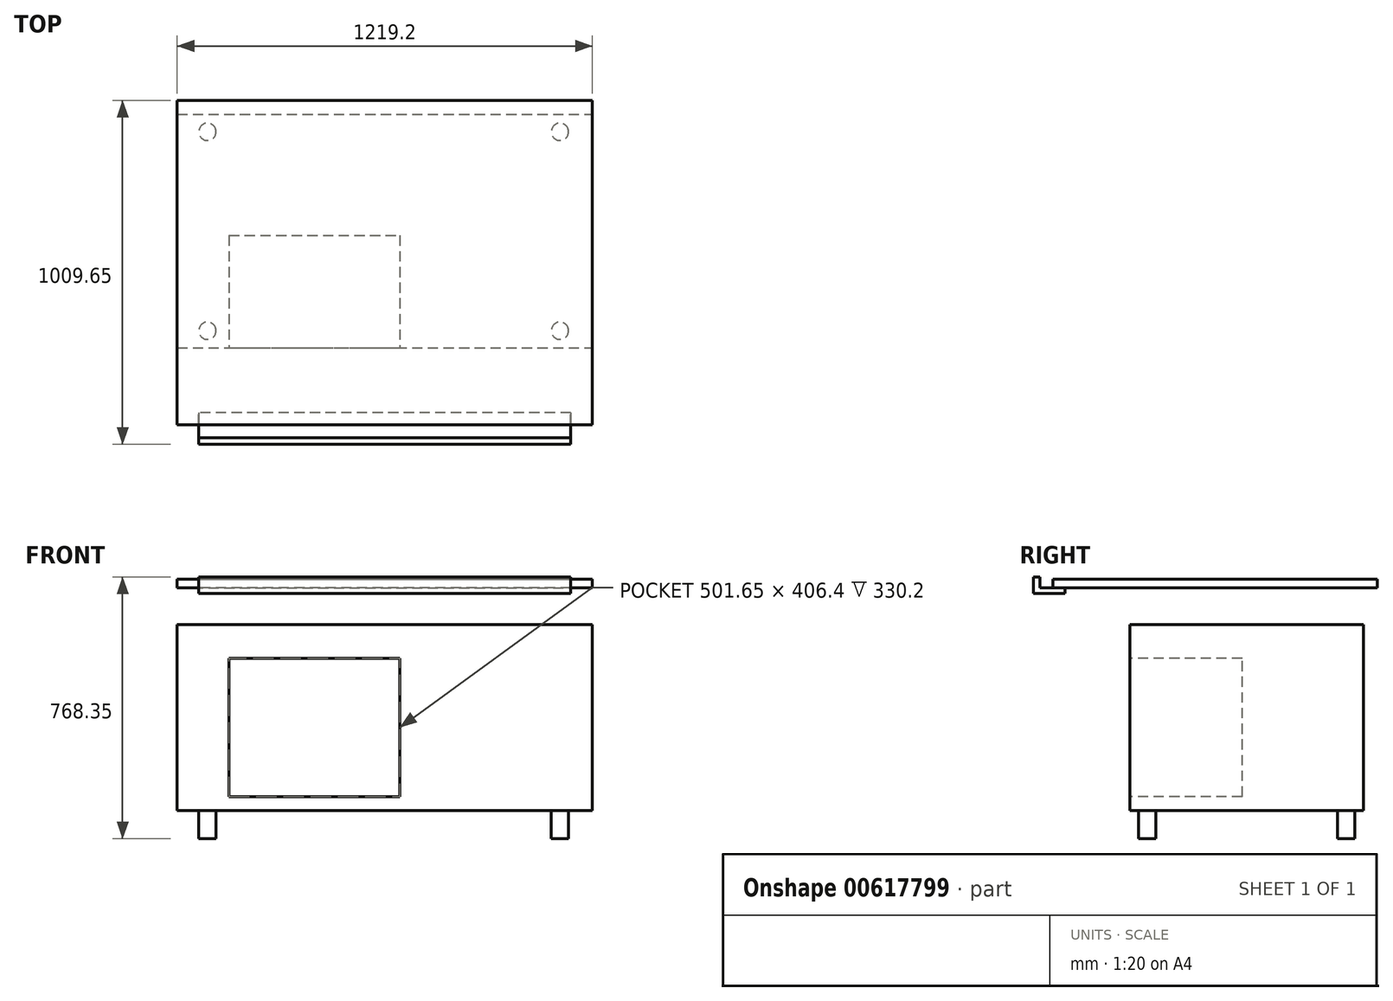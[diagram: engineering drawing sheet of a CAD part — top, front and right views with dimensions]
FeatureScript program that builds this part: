
annotation { "Feature Type Name" : "Feature", "Feature Type Description" : "" }
export const myFeature = defineFeature(function(context is Context, id is Id, definition is map)
    precondition{}
    {
        {
            var Q0;
            Q0=qCreatedBy(makeId("Top.planeOp"),FACE);
            var sketch = newSketch(context, id + "F0", { "sketchPlane" : qUnion([Q0])});
            skCircle(sketch, "E0", {"center": v(1035.05, 0) * mm, "radius": 25.4 * mm});
            skCircle(sketch, "E1", {"center": v(0, 0) * mm, "radius": 25.4 * mm});
            skCircle(sketch, "E2", {"center": v(1035.05, 584.2) * mm, "radius": 25.4 * mm});
            skCircle(sketch, "E3", {"center": v(0, 584.2) * mm, "radius": 25.4 * mm});
            skLineSegment(sketch, "E4.bottom", {"start": v(0, 584.2) * mm, "end": v(1035.05, 584.2) * mm, "construction": true});
            skLineSegment(sketch, "E4.top", {"start": v(0, 0) * mm, "end": v(1035.05, 0) * mm, "construction": true});
            skLineSegment(sketch, "E4.left", {"start": v(0, 584.2) * mm, "end": v(0, 0) * mm, "construction": true});
            skLineSegment(sketch, "E4.right", {"start": v(1035.05, 584.2) * mm, "end": v(1035.05, 0) * mm, "construction": true});
            skSolve(sketch);
        }
        {
            var Q0;
            Q0 = qSketchRegion(id + "F0", true);
            extrude(context, id + "F1", {"entities" : qUnion([Q0]), "depth" : 82.55 * mm, "offsetDistance" : 25.4 * mm});
        }
        {
            var Q0;
            Q0=makeQuery(id+"F1.opExtrude","CAP_FACE",FACE,{"disambiguationData":[OSD([sQuery(id+"F0.wireOp",EDGE,"E3")])],"isStart":false});
            var sketch = newSketch(context, id + "F2", { "sketchPlane" : qUnion([Q0])});
            skLineSegment(sketch, "E5.bottom", {"start": v(-88.9, 635) * mm, "end": v(1130.3, 635) * mm});
            skLineSegment(sketch, "E5.top", {"start": v(-88.9, -50.8) * mm, "end": v(1130.3, -50.8) * mm});
            skLineSegment(sketch, "E5.left", {"start": v(-88.9, 635) * mm, "end": v(-88.9, -50.8) * mm});
            skLineSegment(sketch, "E5.right", {"start": v(1130.3, 635) * mm, "end": v(1130.3, -50.8) * mm});
            skSolve(sketch);
        }
        {
            var Q0;
            Q0 = qSketchRegion(id + "F2", true);
            extrude(context, id + "F3", {"entities" : qUnion([Q0]), "depth" : 546.1 * mm, "offsetDistance" : 25.4 * mm});
        }
        {
            var Q0;
            Q0=makeQuery(id+"F3.opExtrude","SWEPT_FACE",FACE,{"disambiguationData":[OSD([sQuery(id+"F2.wireOp",EDGE,"E5.top")])]});
            var sketch = newSketch(context, id + "F4", { "sketchPlane" : qUnion([Q0])});
            skLineSegment(sketch, "E6.bottom", {"start": v(63.5, 123.83) * mm, "end": v(565.15, 123.83) * mm});
            skLineSegment(sketch, "E6.top", {"start": v(63.5, 530.22) * mm, "end": v(565.15, 530.22) * mm});
            skLineSegment(sketch, "E6.left", {"start": v(63.5, 123.83) * mm, "end": v(63.5, 530.23) * mm});
            skLineSegment(sketch, "E6.right", {"start": v(565.15, 123.83) * mm, "end": v(565.15, 530.23) * mm});
            skSolve(sketch);
        }
        {
            var Q0;
            Q0 = qSketchRegion(id + "F4", true);
            extrude(context, id + "F5", {"entities" : qUnion([Q0]), "operationType" : NewBodyOperationType.REMOVE, "oppositeDirection" : true, "depth" : 330.2 * mm, "offsetDistance" : 25.4 * mm});
        }
        {
            var Q0;
            Q0=qCreatedBy(makeId("Top.planeOp"),FACE);
            cPlane(context, id + "F6", {"entities" : qUnion([Q0]), "cplaneType" : CPlaneType.OFFSET, "offset" : 762 * mm, "width" : 152.4 * mm, "height" : 152.4 * mm});
        }
        {
            var Q0;
            Q0=qCreatedBy(id+"F6.planeOp",FACE);
            var sketch = newSketch(context, id + "F7", { "sketchPlane" : qUnion([Q0])});
            skLineSegment(sketch, "E7.bottom", {"start": v(-88.9, 676.28) * mm, "end": v(1130.3, 676.28) * mm});
            skLineSegment(sketch, "E7.top", {"start": v(-88.9, -276.22) * mm, "end": v(1130.3, -276.22) * mm});
            skLineSegment(sketch, "E7.left", {"start": v(-88.9, 676.28) * mm, "end": v(-88.9, -276.22) * mm});
            skLineSegment(sketch, "E7.right", {"start": v(1130.3, 676.28) * mm, "end": v(1130.3, -276.22) * mm});
            skSolve(sketch);
        }
        {
            var Q0;
            Q0 = qSketchRegion(id + "F7", true);
            extrude(context, id + "F8", {"entities" : qUnion([Q0]), "oppositeDirection" : true, "depth" : 25.4 * mm, "offsetDistance" : 25.4 * mm});
        }
        {
            var Q0;
            Q0=makeQuery(id+"F8.opExtrude","CAP_VERTEX",VERTEX,{"disambiguationData":[OSD([sQuery(id+"F7.wireOp",EDGE,"E7.top"),sQuery(id+"F7.wireOp",EDGE,"E7.left")])],"isStart":false});
            var Q1;
            Q1=makeQuery(id+"F8.opExtrude","CAP_VERTEX",VERTEX,{"disambiguationData":[OSD([sQuery(id+"F7.wireOp",EDGE,"E7.top"),sQuery(id+"F7.wireOp",EDGE,"E7.right")])],"isStart":false});
            cPlane(context, id + "F9", {"entities" : qUnion([Q0, Q1]), "cplaneType" : CPlaneType.MID_PLANE, "offset" : 25.4 * mm, "width" : 152.4 * mm, "height" : 152.4 * mm});
        }
        {
            var Q0;
            Q0=qCreatedBy(id+"F9.planeOp",FACE);
            var sketch = newSketch(context, id + "F10", { "sketchPlane" : qUnion([Q0])});
            skLineSegment(sketch, "E8", {"start": v(-241.3, 736.6) * mm, "end": v(-241.3, 720.73) * mm});
            skLineSegment(sketch, "E9", {"start": v(-241.3, 720.73) * mm, "end": v(-333.38, 720.73) * mm});
            skLineSegment(sketch, "E10", {"start": v(-333.38, 720.73) * mm, "end": v(-333.38, 768.35) * mm});
            skLineSegment(sketch, "E11", {"start": v(-333.38, 768.35) * mm, "end": v(-314.32, 768.35) * mm});
            skLineSegment(sketch, "E12", {"start": v(-314.32, 768.35) * mm, "end": v(-314.32, 736.6) * mm});
            skLineSegment(sketch, "E13", {"start": v(-314.32, 736.6) * mm, "end": v(-241.3, 736.6) * mm});
            skSolve(sketch);
        }
        {
            var Q0;
            Q0 = qSketchRegion(id + "F10", true);
            extrude(context, id + "F11", {"entities" : qUnion([Q0]), "endBound" : BoundingType.SYMMETRIC, "depth" : 1092.2 * mm, "offsetDistance" : 25.4 * mm});
        }
    });
